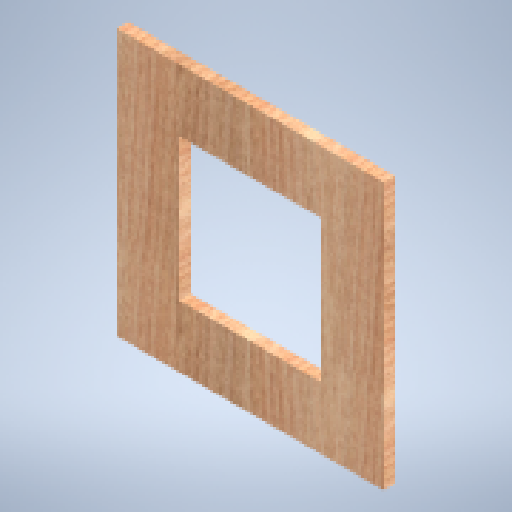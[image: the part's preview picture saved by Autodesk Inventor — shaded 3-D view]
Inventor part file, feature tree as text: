
AUTODESK INVENTOR PART (.ipt)
format: ipt  version: 2025.1 (Build 291241000, 241)  size: 399,872 bytes
history: native  units: in
note: dims shown in document units (in); Inventor stores cm internally (conversion verified against a paired STEP export)
features: extrude x1, sketch x1
ambient origin geometry x8: Origin, YZ Plane, XZ Plane, XY Plane, X Axis, Y Axis, Z Axis, Center Point
bodies: Solid1 (feature_tree)
feature tree (2):
  extrude  "Extrusion1"  Depth=11.811in
  sketch  "Sketch2"  dims[d0=11.811in d1=11.811in d2=6.2992in d3=6.2992in d4=0.5in d5=0.0in]
